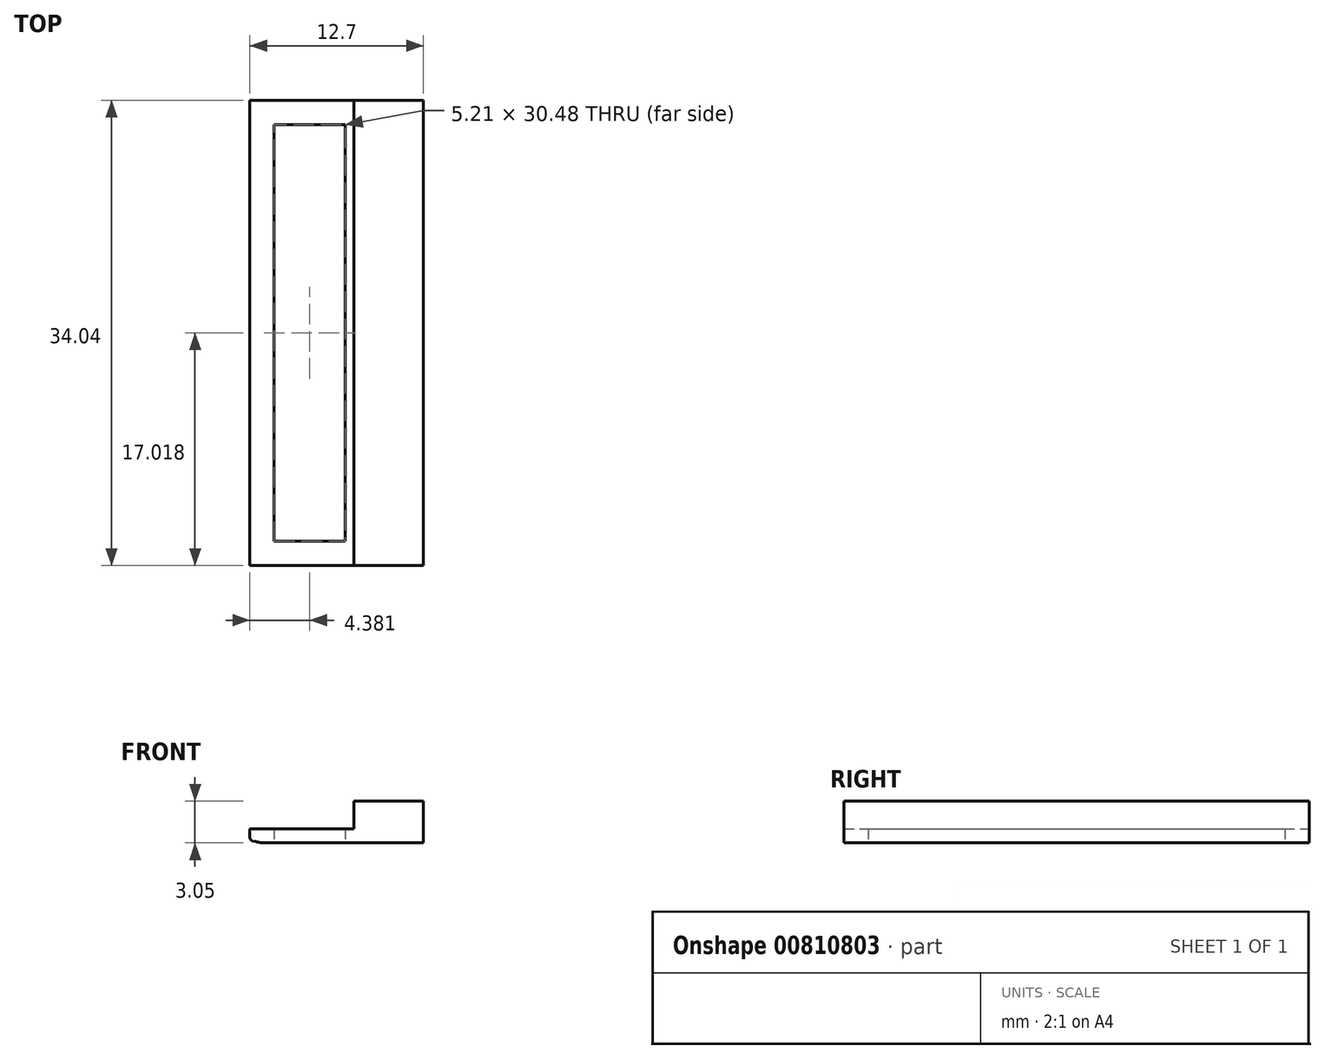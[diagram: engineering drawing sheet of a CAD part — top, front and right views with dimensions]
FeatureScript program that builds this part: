
annotation { "Feature Type Name" : "Feature", "Feature Type Description" : "" }
export const myFeature = defineFeature(function(context is Context, id is Id, definition is map)
    precondition{}
    {
        {
            var Q0;
            Q0=qCreatedBy(makeId("Top.planeOp"),FACE);
            var sketch = newSketch(context, id + "F0", { "sketchPlane" : qUnion([Q0])});
            skLineSegment(sketch, "E0.bottom", {"start": v(0, 0) * mm, "end": v(7.62, 0) * mm});
            skLineSegment(sketch, "E0.top", {"start": v(0, 34.04) * mm, "end": v(7.62, 34.04) * mm});
            skLineSegment(sketch, "E0.left", {"start": v(0, 0) * mm, "end": v(0, 34.04) * mm});
            skLineSegment(sketch, "E0.right", {"start": v(7.62, 0) * mm, "end": v(7.62, 34.04) * mm});
            skLineSegment(sketch, "E1.bottom", {"start": v(1.78, 1.78) * mm, "end": v(6.98, 1.78) * mm});
            skLineSegment(sketch, "E1.top", {"start": v(1.78, 32.26) * mm, "end": v(6.98, 32.26) * mm});
            skLineSegment(sketch, "E1.left", {"start": v(1.78, 1.78) * mm, "end": v(1.78, 32.26) * mm});
            skLineSegment(sketch, "E1.right", {"start": v(6.98, 1.78) * mm, "end": v(6.98, 32.26) * mm});
            skSolve(sketch);
        }
        {
            var Q0;
            Q0 = qSketchRegion(id + "F0", true);
            extrude(context, id + "F1", {"entities" : qUnion([Q0]), "depth" : 1.02 * mm, "offsetDistance" : 25.4 * mm});
        }
        {
            var Q0;
            Q0=makeQuery(id+"F1.opExtrude","CAP_EDGE",EDGE,{"disambiguationData":[OSD([sQuery(id+"F0.wireOp",EDGE,"E0.left")])],"isStart":true});
            chamfer(context, id + "F2", {"entities" : qUnion([Q0]), "chamferType" : ChamferType.OFFSET_ANGLE, "width" : 0.76 * mm, "oppositeDirection" : false, "angle" : 15 * degree, "tangentPropagation" : true});
        }
        {
            var Q0;
            {var subQ0=sQuery(id+"F0.wireOp",EDGE,"E0.left");Q0=makeQuery(id+"F2.opChamfer","BLEND_EDGE",EDGE,{"blendedFrom":[makeQuery(id+"F1.opExtrude","CAP_EDGE",EDGE,{"disambiguationData":[OSD([subQ0])],"isStart":true}),makeQuery(id+"F1.opExtrude","SWEPT_FACE",FACE,{"disambiguationData":[OSD([subQ0])]})],"blendedInto":[makeQuery(id+"F1.opExtrude","SWEPT_FACE",FACE,{"disambiguationData":[OSD([subQ0])]})]});}
            fillet(context, id + "F3", {"entities" : qUnion([Q0]), "radius" : 0.25 * mm, "tangentPropagation" : true, "allowEdgeOverflow" : false});
        }
        {
            var Q0;
            {var subQ0=sQuery(id+"F0.wireOp",EDGE,"E0.left");Q0=makeQuery(id+"F2.opChamfer","BLEND_EDGE",EDGE,{"blendedFrom":[makeQuery(id+"F1.opExtrude","CAP_EDGE",EDGE,{"disambiguationData":[OSD([subQ0])],"isStart":true}),makeQuery(id+"F1.opExtrude","CAP_FACE",FACE,{"disambiguationData":[OSD([sQuery(id+"F0.wireOp",EDGE,"E0.bottom"),sQuery(id+"F0.wireOp",EDGE,"E0.top"),subQ0,sQuery(id+"F0.wireOp",EDGE,"E0.right"),sQuery(id+"F0.wireOp",EDGE,"E1.bottom"),sQuery(id+"F0.wireOp",EDGE,"E1.top"),sQuery(id+"F0.wireOp",EDGE,"E1.left"),sQuery(id+"F0.wireOp",EDGE,"E1.right")])],"isStart":true})],"blendedInto":[makeQuery(id+"F1.opExtrude","CAP_FACE",FACE,{"disambiguationData":[OSD([sQuery(id+"F0.wireOp",EDGE,"E0.bottom"),sQuery(id+"F0.wireOp",EDGE,"E0.top"),subQ0,sQuery(id+"F0.wireOp",EDGE,"E0.right"),sQuery(id+"F0.wireOp",EDGE,"E1.bottom"),sQuery(id+"F0.wireOp",EDGE,"E1.top"),sQuery(id+"F0.wireOp",EDGE,"E1.left"),sQuery(id+"F0.wireOp",EDGE,"E1.right")])],"isStart":true})]});}
            fillet(context, id + "F4", {"entities" : qUnion([Q0]), "radius" : 3.05 * mm, "tangentPropagation" : true, "allowEdgeOverflow" : false});
        }
        {
            var Q0;
            Q0=qCreatedBy(makeId("Top.planeOp"),FACE);
            var sketch = newSketch(context, id + "F5", { "sketchPlane" : qUnion([Q0])});
            skLineSegment(sketch, "E2.bottom", {"start": v(7.62, 0) * mm, "end": v(12.7, 0) * mm});
            skLineSegment(sketch, "E2.top", {"start": v(7.62, 34.04) * mm, "end": v(12.7, 34.04) * mm});
            skLineSegment(sketch, "E2.left", {"start": v(7.62, 0) * mm, "end": v(7.62, 34.04) * mm});
            skLineSegment(sketch, "E2.right", {"start": v(12.7, 0) * mm, "end": v(12.7, 34.04) * mm});
            skSolve(sketch);
        }
        {
            var Q0;
            Q0=makeQuery(id+"F5.imprint","IMPRINT",FACE,{"disambiguationData":[TD([[makeQuery(id+"F5.imprint","IMPRINT",EDGE,{"derivedFrom":sQuery(id+"F5.wireOp",EDGE,"E2.bottom")}),1.0]])]});
            extrude(context, id + "F6", {"entities" : qUnion([Q0]), "operationType" : NewBodyOperationType.ADD, "depth" : 3.05 * mm, "offsetDistance" : 25.4 * mm});
        }
    });
